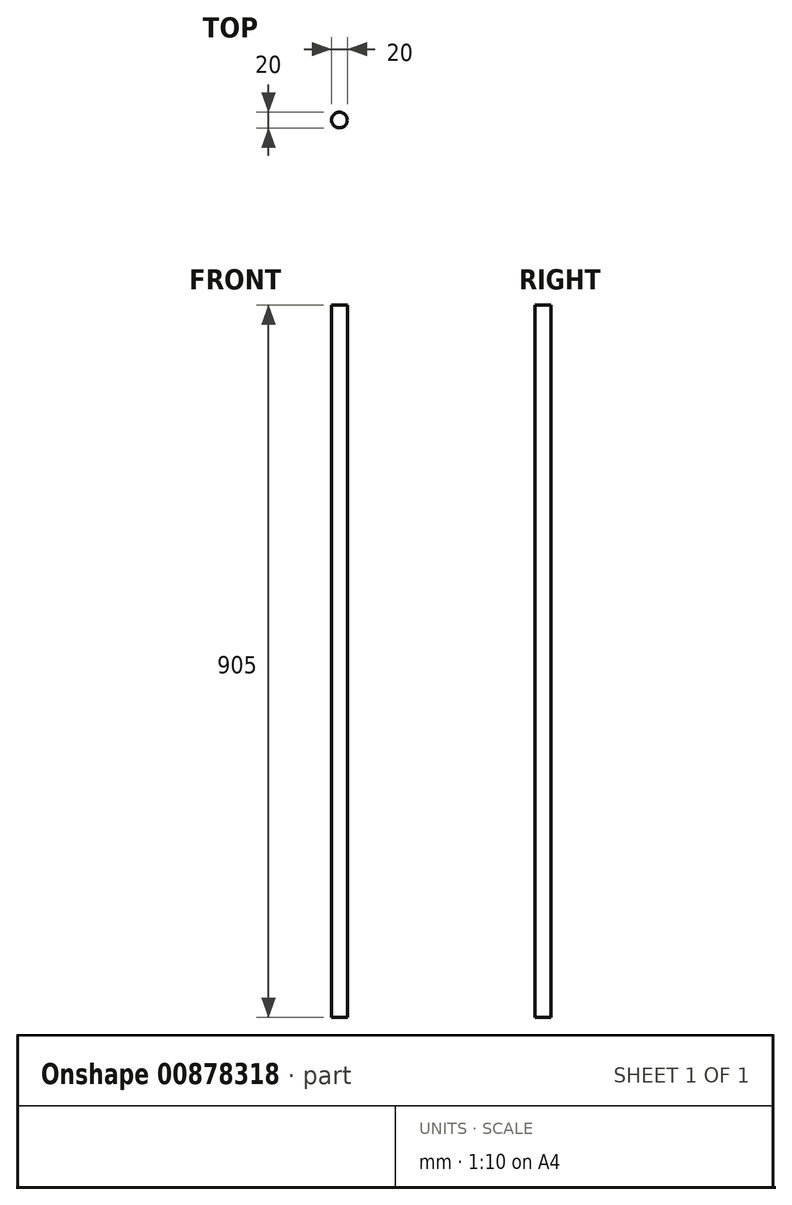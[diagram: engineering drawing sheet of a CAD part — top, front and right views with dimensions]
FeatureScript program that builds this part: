
annotation { "Feature Type Name" : "Feature", "Feature Type Description" : "" }
export const myFeature = defineFeature(function(context is Context, id is Id, definition is map)
    precondition{}
    {
        {
            var Q0;
            Q0=qCreatedBy(makeId("Top.planeOp"),FACE);
            var sketch = newSketch(context, id + "F0", { "sketchPlane" : qUnion([Q0])});
            skCircle(sketch, "E0", {"center": v(0, 0) * mm, "radius": 10 * mm});
            skSolve(sketch);
        }
        {
            var Q0;
            Q0 = qSketchRegion(id + "F0", true);
            extrude(context, id + "F1", {"entities" : qUnion([Q0]), "depth" : 880 * mm, "offsetDistance" : 25 * mm});
        }
        {
            var Q0;
            Q0=makeQuery(id+"F1.opExtrude","CAP_FACE",FACE,{"disambiguationData":[OSD([sQuery(id+"F0.wireOp",EDGE,"E0")])],"isStart":false});
            var sketch = newSketch(context, id + "F2", { "sketchPlane" : qUnion([Q0])});
            skCircle(sketch, "E1", {"center": v(0, 0) * mm, "radius": 1.7 * mm});
            skSolve(sketch);
        }
        {
            var Q0;
            Q0=makeQuery(id+"F2.imprint","IMPRINT",FACE,{"disambiguationData":[TD([[makeQuery(id+"F2.imprint","IMPRINT",EDGE,{"derivedFrom":sQuery(id+"F2.wireOp",EDGE,"E1")}),1.0]])]});
            var Q1;
            Q1=makeQuery(id+"F2.imprint","IMPRINT",FACE,{"disambiguationData":[TD([[makeQuery(id+"F2.imprint","IMPRINT",EDGE,{"derivedFrom":sQuery(id+"F2.wireOp",EDGE,"E1")}),-1.0]])]});
            var Q2;
            Q2=makeQuery(id+"F1.opExtrude","CAP_FACE",FACE,{"disambiguationData":[OSD([sQuery(id+"F0.wireOp",EDGE,"E0")])],"isStart":false});
            extrude(context, id + "F3", {"entities" : qUnion([Q0, Q1, Q2]), "operationType" : NewBodyOperationType.ADD, "depth" : 25 * mm, "offsetDistance" : 25 * mm});
        }
    });
